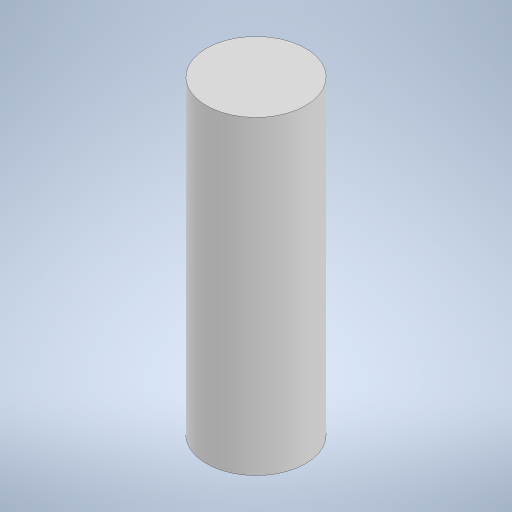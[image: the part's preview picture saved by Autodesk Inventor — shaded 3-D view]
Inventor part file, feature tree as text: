
AUTODESK INVENTOR PART (.ipt)
format: ipt  version: 2024.2 (Build 282272000, 272)  size: 216,064 bytes
history: native  units: mm
features: extrude x1, sketch x1
ambient origin geometry x8: Origin, YZ Plane, XZ Plane, XY Plane, X Axis, Y Axis, Z Axis, Center Point
bodies: Solid1 (feature_tree)
feature tree (2):
  extrude  "Extrusion1"  Depth=10.0mm TaperAngle=0.0deg
  sketch  "Sketch1"  dims[d0=3.2mm d1=10.0mm d2=0.0mm]
